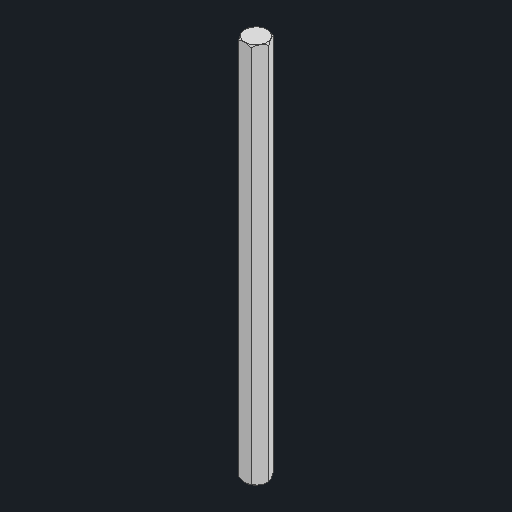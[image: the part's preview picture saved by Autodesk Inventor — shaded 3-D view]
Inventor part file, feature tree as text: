
AUTODESK INVENTOR PART (.ipt)
format: ipt  version: 2023 (Build 270158000, 158)  size: 107,520 bytes
history: native  units: in
note: dims shown in document units (in); Inventor stores cm internally (conversion verified against a paired STEP export)
features: mirror x1
ambient origin geometry x8: Origin, YZ Plane, XZ Plane, XY Plane, X Axis, Y Axis, Z Axis, Center Point
bodies: Solid1 (feature_tree)
feature tree (1):
  mirror  "Mirror1"
